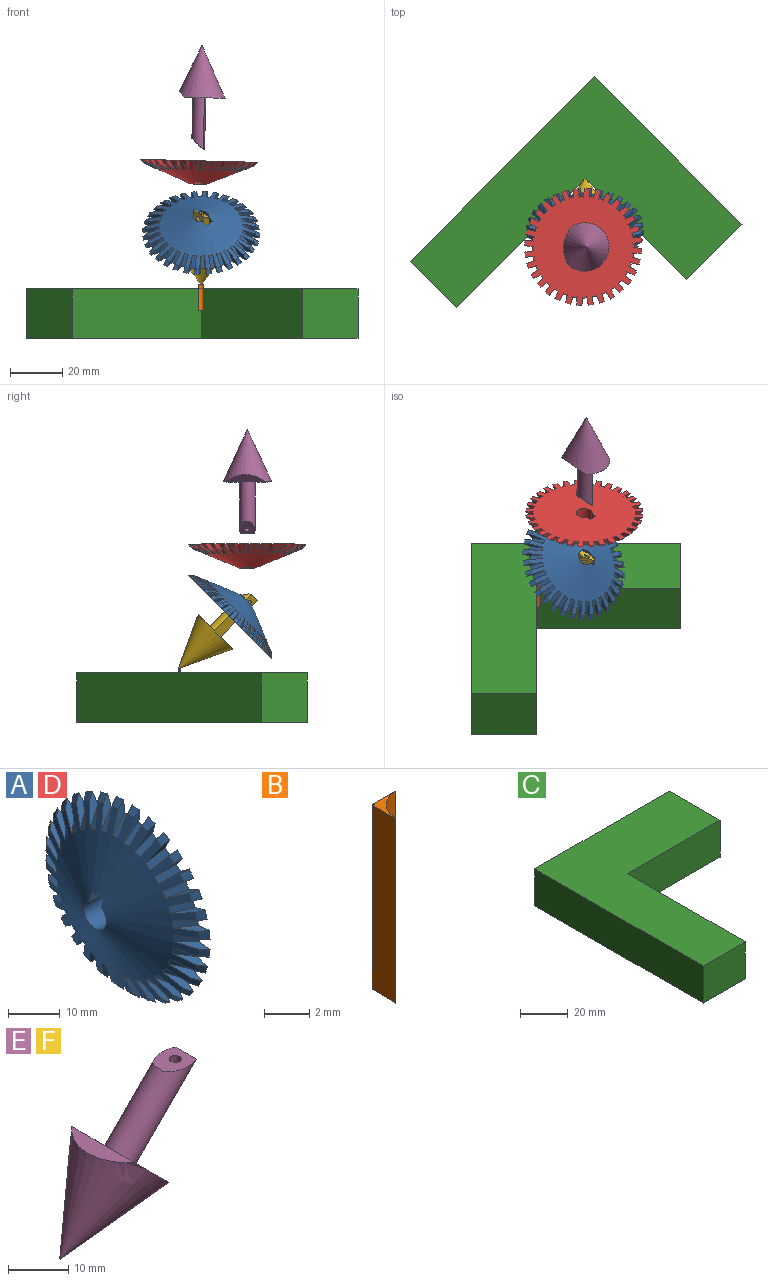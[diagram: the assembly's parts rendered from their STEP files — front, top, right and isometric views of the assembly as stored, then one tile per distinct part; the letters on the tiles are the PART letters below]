
ASSEMBLY  parts=6 mates=4
PART A: 198 faces, bbox 9x45x45 mm
  f0: plane 8.28x3.13mm, normal (0,0,-1), area 25.8mm2, adj f194,f195,f196,f197
  f1: revolved ~2.25x1.63mm, area 3.8mm2, adj f34,f46,f196,f197
  f2: revolved ~2.04x1.66mm, area 3.8mm2, adj f50,f192,f196,f197
  f3: revolved ~2.19x2.01mm, area 3.8mm2, adj f184,f189,f196,f197
  f4: revolved ~2.47x2.35mm, area 3.8mm2, adj f175,f179,f196,f197
  f5: revolved ~2.32x2.28mm, area 3.8mm2, adj f173,f183,f196,f197
  f6: revolved ~2.45x1.93mm, area 3.8mm2, adj f154,f169,f196,f197
  f7: revolved ~2.25x1.63mm, area 3.8mm2, adj f164,f168,f196,f197
  f8: revolved ~2.55x2.16mm, area 3.8mm2, adj f153,f160,f196,f197
  f9: revolved ~2.56x2.3mm, area 3.8mm2, adj f158,f178,f196,f197
  f10: revolved ~2.56x2.3mm, area 3.8mm2, adj f130,f149,f196,f197
  f11: revolved ~2.55x2.16mm, area 3.8mm2, adj f144,f148,f196,f197
  f12: revolved ~2.45x1.93mm, area 3.8mm2, adj f33,f143,f196,f197
  f13: revolved ~2.32x2.28mm, area 3.8mm2, adj f134,f139,f196,f197
  f14: revolved ~2.47x2.35mm, area 3.8mm2, adj f128,f138,f196,f197
  f15: revolved ~2.19x2.01mm, area 3.8mm2, adj f125,f133,f196,f197
  f16: revolved ~2.04x1.66mm, area 3.8mm2, adj f123,f163,f196,f197
  f17: revolved ~2.04x1.66mm, area 3.8mm2, adj f54,f119,f196,f197
  f18: revolved ~2.19x2.01mm, area 3.8mm2, adj f114,f118,f196,f197
  f19: revolved ~2.47x2.35mm, area 3.8mm2, adj f105,f109,f196,f197
  f20: revolved ~2.32x2.28mm, area 3.8mm2, adj f103,f113,f196,f197
  f21: revolved ~2.45x1.93mm, area 3.8mm2, adj f89,f99,f196,f197
  f22: revolved ~2.25x1.63mm, area 3.8mm2, adj f48,f98,f196,f197
  f23: revolved ~2.55x2.16mm, area 3.8mm2, adj f88,f95,f196,f197
  f24: revolved ~2.56x2.3mm, area 3.8mm2, adj f93,f108,f196,f197
  f25: revolved ~2.56x2.3mm, area 3.8mm2, adj f60,f84,f196,f197
  f26: revolved ~2.55x2.16mm, area 3.8mm2, adj f79,f83,f196,f197
  f27: revolved ~2.25x1.63mm, area 3.8mm2, adj f53,f75,f196,f197
  f28: revolved ~2.45x1.93mm, area 3.8mm2, adj f73,f78,f196,f197
  f29: revolved ~2.32x2.28mm, area 3.8mm2, adj f64,f69,f196,f197
  f30: revolved ~2.47x2.35mm, area 3.8mm2, adj f58,f68,f196,f197
  f31: revolved ~2.19x2.01mm, area 3.8mm2, adj f38,f63,f196,f197
  f32: revolved ~2.04x1.66mm, area 3.8mm2, adj f39,f47,f196,f197
  f33: plane 1.53x1.51mm, normal (0.01,-0.98,0.21), area 0.1mm2, adj f12,f37,f196,f197
  f34: plane 1.54x1.51mm, normal (0.01,0.98,-0.19), area 0.1mm2, adj f1,f35,f196,f197
  f35: plane 6.34x3.54mm, normal (-0.11,0.99,-0.06), area 7.2mm2, adj f34,f36,f196,f197
  f36: plane 3.83x3.6mm, normal (-0.71,0.14,0.69), area 8mm2, adj f35,f37,f196,f197
  f37: plane 6.16x3.54mm, normal (-0.11,-0.94,0.32), area 7.2mm2, adj f33,f36,f196,f197
  f38: plane 1.53x1.51mm, normal (0.01,0.98,0.21), area 0.1mm2, adj f31,f42,f196,f197
  f39: plane 1.55x1.51mm, normal (0.01,-0.98,-0.19), area 0.1mm2, adj f32,f40,f196,f197
  f40: plane 6.34x3.54mm, normal (-0.11,-0.99,-0.06), area 7.2mm2, adj f39,f41,f196,f197
  f41: plane 3.83x3.6mm, normal (-0.71,-0.14,0.69), area 8mm2, adj f40,f42,f196,f197
  f42: plane 6.16x3.54mm, normal (-0.11,0.94,0.32), area 7.2mm2, adj f38,f41,f196,f197
  f43: plane 6.37x3.54mm, normal (-0.11,0.98,0.13), area 7.2mm2, adj f45,f47,f196,f197
  f44: plane 6.37x3.54mm, normal (-0.11,-0.98,0.13), area 7.2mm2, adj f45,f46,f196,f197
  f45: plane 3.6x3.6mm, normal (-0.71,0,0.71), area 8mm2, adj f43,f44,f196,f197
  f46: plane 1.57x1.51mm, normal (0.01,-1,0.01), area 0.1mm2, adj f1,f44,f196,f197
  f47: plane 1.57x1.51mm, normal (0.01,1,0.01), area 0.1mm2, adj f32,f43,f196,f197
  f48: plane 1.57x1.51mm, normal (0.01,1,-0.01), area 0.1mm2, adj f22,f49,f196,f197
  f49: plane 6.37x3.54mm, normal (-0.11,0.98,-0.13), area 7.2mm2, adj f48,f52,f196,f197
  f50: plane 1.57x1.51mm, normal (0.01,-1,-0.01), area 0.1mm2, adj f2,f51,f196,f197
  f51: plane 6.37x3.54mm, normal (-0.11,-0.98,-0.13), area 7.2mm2, adj f50,f52,f196,f197
  f52: plane 3.6x3.6mm, normal (-0.71,0,-0.71), area 8mm2, adj f49,f51,f196,f197
  f53: plane 1.57x1.51mm, normal (0.01,-0.01,-1), area 0.1mm2, adj f27,f57,f196,f197
  f54: plane 1.57x1.51mm, normal (0.01,-0.01,1), area 0.1mm2, adj f17,f55,f196,f197
  f55: plane 6.37x3.54mm, normal (-0.11,-0.13,0.98), area 7.2mm2, adj f54,f56,f196,f197
  f56: plane 3.6x3.6mm, normal (-0.71,-0.71,0), area 8mm2, adj f55,f57,f196,f197
  f57: plane 6.37x3.54mm, normal (-0.11,-0.13,-0.98), area 7.2mm2, adj f53,f56,f196,f197
  f58: plane 1.51x1.13mm, normal (0.01,-0.71,-0.7), area 0.1mm2, adj f30,f59,f196,f197
  f59: plane 4.83x4.19mm, normal (-0.11,-0.79,-0.6), area 7.2mm2, adj f58,f62,f196,f197
  f60: plane 1.51x1.13mm, normal (0.01,0.7,0.71), area 0.1mm2, adj f25,f61,f196,f197
  f61: plane 4.83x4.19mm, normal (-0.11,0.6,0.79), area 7.2mm2, adj f60,f62,f196,f197
  f62: plane 3.7x3.7mm, normal (-0.71,-0.5,0.5), area 8mm2, adj f59,f61,f196,f197
  f63: plane 1.51x1.46mm, normal (0.01,-0.93,-0.37), area 0.1mm2, adj f31,f67,f196,f197
  f64: plane 1.51x1.44mm, normal (0.01,0.92,0.39), area 0.1mm2, adj f29,f65,f196,f197
  f65: plane 5.71x3.54mm, normal (-0.11,0.86,0.5), area 7.2mm2, adj f64,f66,f196,f197
  f66: plane 3.94x3.6mm, normal (-0.71,-0.27,0.65), area 8mm2, adj f65,f67,f196,f197
  f67: plane 6.06x3.54mm, normal (-0.11,-0.96,-0.25), area 7.2mm2, adj f63,f66,f196,f197
  f68: plane 1.51x1.29mm, normal (0.01,0.83,0.56), area 0.1mm2, adj f30,f72,f196,f197
  f69: plane 1.51x1.32mm, normal (0.01,-0.84,-0.55), area 0.1mm2, adj f29,f71,f196,f197
  f70: plane 3.89x3.6mm, normal (-0.71,-0.39,0.59), area 8mm2, adj f71,f72,f196,f197
  f71: plane 5.55x3.54mm, normal (-0.11,-0.89,-0.44), area 7.2mm2, adj f69,f70,f196,f197
  f72: plane 5.05x3.92mm, normal (-0.11,0.74,0.66), area 7.2mm2, adj f68,f70,f196,f197
  f73: plane 1.53x1.51mm, normal (0.01,-0.21,-0.98), area 0.1mm2, adj f28,f74,f196,f197
  f74: plane 6.16x3.54mm, normal (-0.11,-0.32,-0.94), area 7.2mm2, adj f73,f77,f196,f197
  f75: plane 1.54x1.51mm, normal (0.01,0.19,0.98), area 0.1mm2, adj f27,f76,f196,f197
  f76: plane 6.34x3.54mm, normal (-0.11,0.06,0.99), area 7.2mm2, adj f75,f77,f196,f197
  f77: plane 3.83x3.6mm, normal (-0.71,-0.69,0.14), area 8mm2, adj f74,f76,f196,f197
  f78: plane 1.51x1.46mm, normal (0.01,0.37,0.93), area 0.1mm2, adj f28,f82,f196,f197
  f79: plane 1.51x1.44mm, normal (0.01,-0.39,-0.92), area 0.1mm2, adj f26,f80,f196,f197
  f80: plane 5.71x3.54mm, normal (-0.11,-0.5,-0.86), area 7.2mm2, adj f79,f81,f196,f197
  f81: plane 3.94x3.6mm, normal (-0.71,-0.65,0.27), area 8mm2, adj f80,f82,f196,f197
  f82: plane 6.06x3.54mm, normal (-0.11,0.25,0.96), area 7.2mm2, adj f78,f81,f196,f197
  f83: plane 1.51x1.32mm, normal (0.01,0.55,0.84), area 0.1mm2, adj f26,f87,f196,f197
  f84: plane 1.51x1.29mm, normal (0.01,-0.56,-0.83), area 0.1mm2, adj f25,f86,f196,f197
  f85: plane 3.89x3.6mm, normal (-0.71,-0.59,0.39), area 8mm2, adj f86,f87,f196,f197
  f86: plane 5.05x3.92mm, normal (-0.11,-0.66,-0.74), area 7.2mm2, adj f84,f85,f196,f197
  f87: plane 5.55x3.54mm, normal (-0.11,0.44,0.89), area 7.2mm2, adj f83,f85,f196,f197
  f88: plane 1.51x1.44mm, normal (0.01,0.92,-0.39), area 0.1mm2, adj f23,f92,f196,f197
  f89: plane 1.51x1.46mm, normal (0.01,-0.93,0.37), area 0.1mm2, adj f21,f90,f196,f197
  f90: plane 6.06x3.54mm, normal (-0.11,-0.96,0.25), area 7.2mm2, adj f89,f91,f196,f197
  f91: plane 3.94x3.6mm, normal (-0.71,-0.27,-0.65), area 8mm2, adj f90,f92,f196,f197
  f92: plane 5.71x3.54mm, normal (-0.11,0.86,-0.5), area 7.2mm2, adj f88,f91,f196,f197
  f93: plane 1.51x1.29mm, normal (0.01,0.83,-0.56), area 0.1mm2, adj f24,f94,f196,f197
  f94: plane 5.05x3.92mm, normal (-0.11,0.74,-0.66), area 7.2mm2, adj f93,f97,f196,f197
  f95: plane 1.51x1.32mm, normal (0.01,-0.84,0.55), area 0.1mm2, adj f23,f96,f196,f197
  f96: plane 5.55x3.54mm, normal (-0.11,-0.89,0.44), area 7.2mm2, adj f95,f97,f196,f197
  f97: plane 3.89x3.6mm, normal (-0.71,-0.39,-0.59), area 8mm2, adj f94,f96,f196,f197
  f98: plane 1.54x1.51mm, normal (0.01,-0.98,0.19), area 0.1mm2, adj f22,f102,f196,f197
  f99: plane 1.53x1.51mm, normal (0.01,0.98,-0.21), area 0.1mm2, adj f21,f101,f196,f197
  f100: plane 3.83x3.6mm, normal (-0.71,-0.14,-0.69), area 8mm2, adj f101,f102,f196,f197
  f101: plane 6.16x3.54mm, normal (-0.11,0.94,-0.32), area 7.2mm2, adj f99,f100,f196,f197
  f102: plane 6.34x3.54mm, normal (-0.11,-0.99,0.06), area 7.2mm2, adj f98,f100,f196,f197
  f103: plane 1.51x1.32mm, normal (0.01,0.55,-0.84), area 0.1mm2, adj f20,f104,f196,f197
  f104: plane 5.55x3.54mm, normal (-0.11,0.44,-0.89), area 7.2mm2, adj f103,f107,f196,f197
  f105: plane 1.51x1.29mm, normal (0.01,-0.56,0.83), area 0.1mm2, adj f19,f106,f196,f197
  f106: plane 5.05x3.92mm, normal (-0.11,-0.66,0.74), area 7.2mm2, adj f105,f107,f196,f197
  f107: plane 3.89x3.6mm, normal (-0.71,-0.59,-0.39), area 8mm2, adj f104,f106,f196,f197
  f108: plane 1.51x1.13mm, normal (0.01,-0.71,0.7), area 0.1mm2, adj f24,f112,f196,f197
  f109: plane 1.51x1.13mm, normal (0.01,0.7,-0.71), area 0.1mm2, adj f19,f111,f196,f197
  f110: plane 3.7x3.7mm, normal (-0.71,-0.5,-0.5), area 8mm2, adj f111,f112,f196,f197
  f111: plane 4.83x4.19mm, normal (-0.11,0.6,-0.79), area 7.2mm2, adj f109,f110,f196,f197
  f112: plane 4.83x4.19mm, normal (-0.11,-0.79,0.6), area 7.2mm2, adj f108,f110,f196,f197
  f113: plane 1.51x1.44mm, normal (0.01,-0.39,0.92), area 0.1mm2, adj f20,f117,f196,f197
  f114: plane 1.51x1.46mm, normal (0.01,0.37,-0.93), area 0.1mm2, adj f18,f115,f196,f197
  f115: plane 6.06x3.54mm, normal (-0.11,0.25,-0.96), area 7.2mm2, adj f114,f116,f196,f197
  f116: plane 3.94x3.6mm, normal (-0.71,-0.65,-0.27), area 8mm2, adj f115,f117,f196,f197
  f117: plane 5.71x3.54mm, normal (-0.11,-0.5,0.86), area 7.2mm2, adj f113,f116,f196,f197
  f118: plane 1.53x1.51mm, normal (0.01,-0.21,0.98), area 0.1mm2, adj f18,f122,f196,f197
  f119: plane 1.55x1.51mm, normal (0.01,0.19,-0.98), area 0.1mm2, adj f17,f121,f196,f197
  f120: plane 3.83x3.6mm, normal (-0.71,-0.69,-0.14), area 8mm2, adj f121,f122,f196,f197
  f121: plane 6.34x3.54mm, normal (-0.11,0.06,-0.99), area 7.2mm2, adj f119,f120,f196,f197
  f122: plane 6.16x3.54mm, normal (-0.11,-0.32,0.94), area 7.2mm2, adj f118,f120,f196,f197
  f123: plane 1.55x1.51mm, normal (0.01,-0.19,0.98), area 0.1mm2, adj f16,f124,f196,f197
  f124: plane 6.34x3.54mm, normal (-0.11,-0.06,0.99), area 7.2mm2, adj f123,f127,f196,f197
  f125: plane 1.53x1.51mm, normal (0.01,0.21,-0.98), area 0.1mm2, adj f15,f126,f196,f197
  f126: plane 6.16x3.54mm, normal (-0.11,0.32,-0.94), area 7.2mm2, adj f125,f127,f196,f197
  f127: plane 3.83x3.6mm, normal (-0.71,0.69,0.14), area 8mm2, adj f124,f126,f196,f197
  f128: plane 1.51x1.13mm, normal (0.01,-0.7,0.71), area 0.1mm2, adj f14,f129,f196,f197
  f129: plane 4.83x4.19mm, normal (-0.11,-0.6,0.79), area 7.2mm2, adj f128,f132,f196,f197
  f130: plane 1.51x1.13mm, normal (0.01,0.71,-0.7), area 0.1mm2, adj f10,f131,f196,f197
  f131: plane 4.83x4.19mm, normal (-0.11,0.79,-0.6), area 7.2mm2, adj f130,f132,f196,f197
  f132: plane 3.7x3.7mm, normal (-0.71,0.5,0.5), area 8mm2, adj f129,f131,f196,f197
  f133: plane 1.51x1.46mm, normal (0.01,-0.37,0.93), area 0.1mm2, adj f15,f137,f196,f197
  f134: plane 1.51x1.44mm, normal (0.01,0.39,-0.92), area 0.1mm2, adj f13,f135,f196,f197
  f135: plane 5.71x3.54mm, normal (-0.11,0.5,-0.86), area 7.2mm2, adj f134,f136,f196,f197
  f136: plane 3.94x3.6mm, normal (-0.71,0.65,0.27), area 8mm2, adj f135,f137,f196,f197
  f137: plane 6.06x3.54mm, normal (-0.11,-0.25,0.96), area 7.2mm2, adj f133,f136,f196,f197
  f138: plane 1.51x1.29mm, normal (0.01,0.56,-0.83), area 0.1mm2, adj f14,f142,f196,f197
  f139: plane 1.51x1.32mm, normal (0.01,-0.55,0.84), area 0.1mm2, adj f13,f141,f196,f197
  f140: plane 3.89x3.6mm, normal (-0.71,0.59,0.39), area 8mm2, adj f141,f142,f196,f197
  f141: plane 5.55x3.54mm, normal (-0.11,-0.44,0.89), area 7.2mm2, adj f139,f140,f196,f197
  f142: plane 5.05x3.92mm, normal (-0.11,0.66,-0.74), area 7.2mm2, adj f138,f140,f196,f197
  f143: plane 1.51x1.46mm, normal (0.01,0.93,-0.37), area 0.1mm2, adj f12,f147,f196,f197
  f144: plane 1.51x1.44mm, normal (0.01,-0.92,0.39), area 0.1mm2, adj f11,f145,f196,f197
  f145: plane 5.71x3.54mm, normal (-0.11,-0.86,0.5), area 7.2mm2, adj f144,f146,f196,f197
  f146: plane 3.94x3.6mm, normal (-0.71,0.27,0.65), area 8mm2, adj f145,f147,f196,f197
  f147: plane 6.06x3.54mm, normal (-0.11,0.96,-0.25), area 7.2mm2, adj f143,f146,f196,f197
  f148: plane 1.51x1.32mm, normal (0.01,0.84,-0.55), area 0.1mm2, adj f11,f152,f196,f197
  f149: plane 1.51x1.29mm, normal (0.01,-0.83,0.56), area 0.1mm2, adj f10,f151,f196,f197
  f150: plane 3.89x3.6mm, normal (-0.71,0.39,0.59), area 8mm2, adj f151,f152,f196,f197
  f151: plane 5.05x3.92mm, normal (-0.11,-0.74,0.66), area 7.2mm2, adj f149,f150,f196,f197
  f152: plane 5.55x3.54mm, normal (-0.11,0.89,-0.44), area 7.2mm2, adj f148,f150,f196,f197
  f153: plane 1.51x1.44mm, normal (0.01,0.39,0.92), area 0.1mm2, adj f8,f157,f196,f197
  f154: plane 1.51x1.46mm, normal (0.01,-0.37,-0.93), area 0.1mm2, adj f6,f155,f196,f197
  f155: plane 6.06x3.54mm, normal (-0.11,-0.25,-0.96), area 7.2mm2, adj f154,f156,f196,f197
  f156: plane 3.94x3.6mm, normal (-0.71,0.65,-0.27), area 8mm2, adj f155,f157,f196,f197
  f157: plane 5.71x3.54mm, normal (-0.11,0.5,0.86), area 7.2mm2, adj f153,f156,f196,f197
  f158: plane 1.51x1.29mm, normal (0.01,0.56,0.83), area 0.1mm2, adj f9,f159,f196,f197
  f159: plane 5.05x3.92mm, normal (-0.11,0.66,0.74), area 7.2mm2, adj f158,f162,f196,f197
  f160: plane 1.51x1.32mm, normal (0.01,-0.55,-0.84), area 0.1mm2, adj f8,f161,f196,f197
  f161: plane 5.55x3.54mm, normal (-0.11,-0.44,-0.89), area 7.2mm2, adj f160,f162,f196,f197
  f162: plane 3.89x3.6mm, normal (-0.71,0.59,-0.39), area 8mm2, adj f159,f161,f196,f197
  f163: plane 1.57x1.51mm, normal (0.01,0.01,-1), area 0.1mm2, adj f16,f167,f196,f197
  f164: plane 1.57x1.51mm, normal (0.01,0.01,1), area 0.1mm2, adj f7,f165,f196,f197
  f165: plane 6.37x3.54mm, normal (-0.11,0.13,0.98), area 7.2mm2, adj f164,f166,f196,f197
  f166: plane 3.6x3.6mm, normal (-0.71,0.71,0), area 8mm2, adj f165,f167,f196,f197
  f167: plane 6.37x3.54mm, normal (-0.11,0.13,-0.98), area 7.2mm2, adj f163,f166,f196,f197
  f168: plane 1.54x1.51mm, normal (0.01,-0.19,-0.98), area 0.1mm2, adj f7,f172,f196,f197
  f169: plane 1.53x1.51mm, normal (0.01,0.21,0.98), area 0.1mm2, adj f6,f171,f196,f197
  f170: plane 3.83x3.6mm, normal (-0.71,0.69,-0.14), area 8mm2, adj f171,f172,f196,f197
  f171: plane 6.16x3.54mm, normal (-0.11,0.32,0.94), area 7.2mm2, adj f169,f170,f196,f197
  f172: plane 6.34x3.54mm, normal (-0.11,-0.06,-0.99), area 7.2mm2, adj f168,f170,f196,f197
  f173: plane 1.51x1.32mm, normal (0.01,0.84,0.55), area 0.1mm2, adj f5,f174,f196,f197
  f174: plane 5.55x3.54mm, normal (-0.11,0.89,0.44), area 7.2mm2, adj f173,f177,f196,f197
  f175: plane 1.51x1.29mm, normal (0.01,-0.83,-0.56), area 0.1mm2, adj f4,f176,f196,f197
  f176: plane 5.05x3.92mm, normal (-0.11,-0.74,-0.66), area 7.2mm2, adj f175,f177,f196,f197
  f177: plane 3.89x3.6mm, normal (-0.71,0.39,-0.59), area 8mm2, adj f174,f176,f196,f197
  f178: plane 1.51x1.13mm, normal (0.01,-0.7,-0.71), area 0.1mm2, adj f9,f182,f196,f197
  f179: plane 1.51x1.13mm, normal (0.01,0.71,0.7), area 0.1mm2, adj f4,f181,f196,f197
  f180: plane 3.7x3.7mm, normal (-0.71,0.5,-0.5), area 8mm2, adj f181,f182,f196,f197
  f181: plane 4.83x4.19mm, normal (-0.11,0.79,0.6), area 7.2mm2, adj f179,f180,f196,f197
  f182: plane 4.83x4.19mm, normal (-0.11,-0.6,-0.79), area 7.2mm2, adj f178,f180,f196,f197
  f183: plane 1.51x1.44mm, normal (0.01,-0.92,-0.39), area 0.1mm2, adj f5,f187,f196,f197
  f184: plane 1.51x1.46mm, normal (0.01,0.93,0.37), area 0.1mm2, adj f3,f185,f196,f197
  f185: plane 6.06x3.54mm, normal (-0.11,0.96,0.25), area 7.2mm2, adj f184,f186,f196,f197
  f186: plane 3.94x3.6mm, normal (-0.71,0.27,-0.65), area 8mm2, adj f185,f187,f196,f197
  f187: plane 5.71x3.54mm, normal (-0.11,-0.86,-0.5), area 7.2mm2, adj f183,f186,f196,f197
  f188: plane 6.16x3.54mm, normal (-0.11,-0.94,-0.32), area 7.2mm2, adj f189,f191,f196,f197
  f189: plane 1.53x1.51mm, normal (0.01,-0.98,-0.21), area 0.1mm2, adj f3,f188,f196,f197
  f190: plane 6.34x3.54mm, normal (-0.11,0.99,0.06), area 7.2mm2, adj f191,f192,f196,f197
  f191: plane 3.83x3.6mm, normal (-0.71,0.14,-0.69), area 8mm2, adj f188,f190,f196,f197
  f192: plane 1.55x1.51mm, normal (0.01,0.98,0.19), area 0.1mm2, adj f2,f190,f196,f197
  f193: cylinder r=3mm len=8.93mm, axis (-1,0,0), area 138.9mm2, adj f194,f195,f196,f197
  f194: plane 8.93x2mm, normal (0,-1,0), area 17.1mm2, adj f0,f193,f196,f197
  f195: plane 8.93x2mm, normal (0,1,0), area 17.1mm2, adj f0,f193,f196,f197
  f196: plane 44.87x44.87mm, normal (1,0,0), area 1359.7mm2, adj f0,f1,f2,f3,f4,f5,f6,f7
  f197: cone r=0mm half-angle=67.5deg, axis (1,0,0), area 1128.8mm2, adj f0,f1,f2,f3,f4,f5,f6,f7
PART B: 12 faces, bbox 1.5x1.5x10 mm
  f0: plane 9x0.05mm, normal (-1,0,0), area 0.5mm2, adj f1,f3,f6,f7
  f1: plane 9x0.05mm, normal (0,1,0), area 0.4mm2, adj f0,f4,f6,f7
  f2: cylinder r=1.5mm len=10mm, axis (0,0,1), area 23.6mm2, adj f3,f4,f5,f6
  f3: plane 10x1.5mm, normal (0,1,0), area 14.5mm2, adj f0,f2,f4,f5,f6,f7
  f4: plane 10x1.5mm, normal (-1,0,0), area 14.5mm2, adj f1,f2,f3,f5,f6,f7
  f5: plane 1.5x1.5mm, normal (0,0,-1), area 0.5mm2, adj f2,f3,f4
  f6: plane 1.5x1.5mm, normal (0,0,1), area 0.5mm2, adj f0,f1,f2,f3,f4,f8,f9,f10
  f7: plane 0.05x0.05mm, normal (0,0,1), area 0mm2, adj f0,f1,f3,f4
  f8: plane 0.05x0.02mm, normal (-0.87,-0.29,0.41), area 0mm2, adj f6,f9,f11
  f9: plane 0.05x0.02mm, normal (0,0.82,0.58), area 0mm2, adj f6,f8,f10,f11
  f10: plane 0.01x0mm, normal (0.87,0.29,-0.41), area 0mm2, adj f6,f9,f11
  f11: plane 0.04x0.04mm, normal (0.5,-0.5,0.71), area 0mm2, adj f6,f8,f9,f10
PART C: 8 faces, bbox 80x100x19 mm
  f0: plane 70x19mm, normal (1,0,0), area 1330mm2, adj f1,f5,f6,f7
  f1: plane 55x19mm, normal (0,-1,0), area 1045mm2, adj f0,f2,f6,f7
  f2: plane 30x19mm, normal (1,0,0), area 570mm2, adj f1,f3,f6,f7
  f3: plane 80x19mm, normal (0,1,0), area 1520mm2, adj f2,f4,f6,f7
  f4: plane 100x19mm, normal (-1,0,0), area 1900mm2, adj f3,f5,f6,f7
  f5: plane 25x19mm, normal (0,-1,0), area 475mm2, adj f0,f4,f6,f7
  f6: plane 100x80mm, normal (0,0,-1), area 4150mm2, adj f0,f1,f2,f3,f4,f5
  f7: plane 100x80mm, normal (0,0,1), area 4150mm2, adj f0,f1,f2,f3,f4,f5
PART D: same geometry as A
PART E: 9 faces, bbox 29.5x18.7x30.4 mm
  f0: plane 18.65x10.59mm, normal (0.71,0,0.71), area 211.4mm2, adj f1,f3,f4,f5
  f1: cone r=0.02mm half-angle=24.9deg, axis (0.71,0,0.71), area 617.6mm2, adj f0,f2,f5
  f2: plane 0.05x0.03mm, normal (-0.71,0,-0.71), area 0mm2, adj f1
  f3: plane 14.14x14.14mm, normal (0.71,0,-0.71), area 94.2mm2, adj f0,f4,f7,f8
  f4: cylinder r=3mm len=17.47mm, axis (-0.71,0,-0.71), area 224.5mm2, adj f0,f3,f6,f7
  f5: plane 14.83x3.54mm, normal (0,0,1), area 35.6mm2, adj f0,f1
  f6: plane 1.92x0.22mm, normal (1,0,0), area 0.3mm2, adj f4,f7
  f7: plane 6.44x6mm, normal (0,0,1), area 30.2mm2, adj f3,f4,f6,f8
  f8: cylinder r=1mm len=3.43mm, axis (0,0,1), area 15.2mm2, adj f3,f7
PART F: same geometry as E
PLACE A rot(axis=(0.57,0.82,0.01),119deg) t=(67.18,11.07,22.29)mm
PLACE B rot(axis=(0,0,-1),45deg) t=(0,0,1.61)mm
PLACE C rot(axis=(0,0,-1),45deg) t=(0,0,0)mm fixed
PLACE D rot(axis=(0.59,-0.56,0.58),120.3deg) t=(66.34,5.31,47.93)mm
PLACE E rot(axis=(-0.92,0.05,0.39),177.7deg) t=(67.5,5.29,93.31)mm fixed
PLACE F rot(axis=(-0.21,0.21,-0.96),123.5deg) t=(67.18,31.75,1.61)mm
MATE fastened A.f193 <-> F.f1  axis (0,-0.71,0.71) through (67.18,5.59,27.78)mm
MATE cylindrical D.f193 <-> E.f4  axis (0.03,0,1) through (66.37,5.31,49.1)mm
MATE revolute B.f11 <-> F.f4  axis (0,-0.71,0.71) through (67.18,31.75,1.61)mm
MATE slider B.f5 <-> C.f6  axis (0,0,-1) through (67.18,31.82,-8.39)mm
